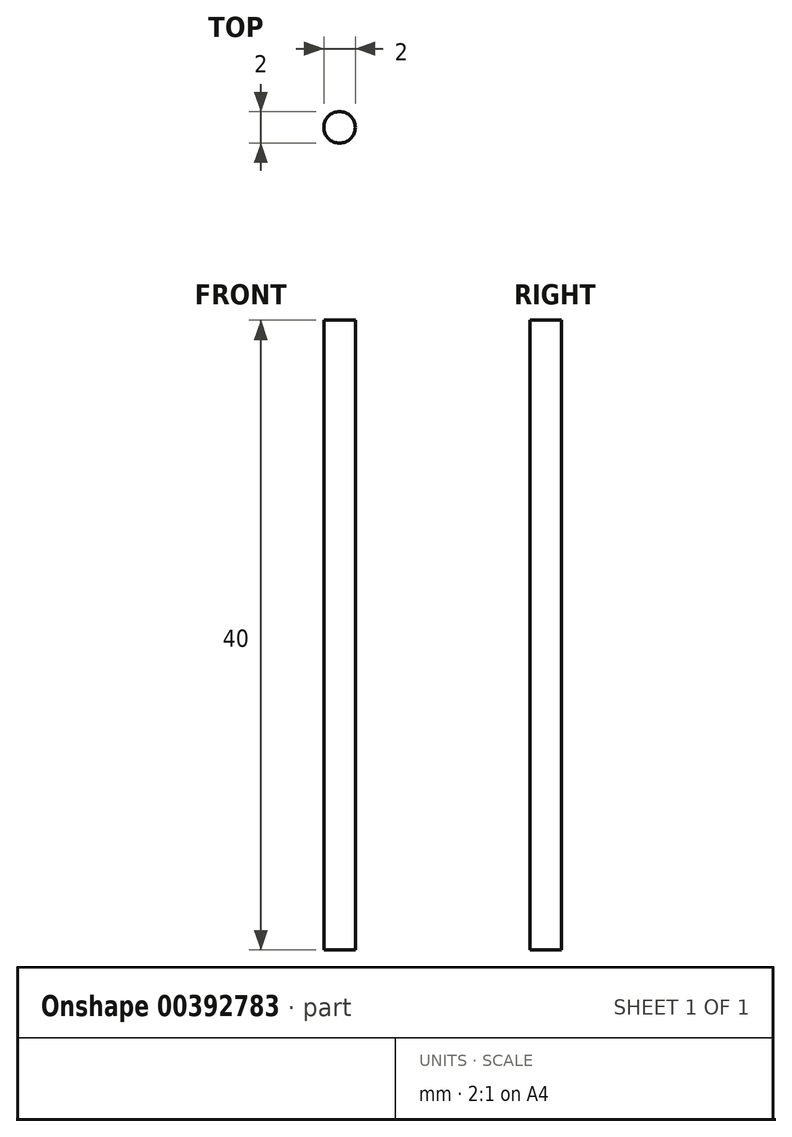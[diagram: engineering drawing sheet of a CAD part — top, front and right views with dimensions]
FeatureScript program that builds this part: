
annotation { "Feature Type Name" : "Feature", "Feature Type Description" : "" }
export const myFeature = defineFeature(function(context is Context, id is Id, definition is map)
    precondition{}
    {
        {
            var Q0;
            Q0=qCreatedBy(makeId("Top.planeOp"),FACE);
            var sketch = newSketch(context, id + "F0", { "sketchPlane" : qUnion([Q0])});
            skCircle(sketch, "E0", {"center": v(0, 0) * mm, "radius": 1 * mm});
            skSolve(sketch);
        }
        {
            var Q0;
            Q0 = qSketchRegion(id + "F0", true);
            extrude(context, id + "F1", {"entities" : qUnion([Q0]), "depth" : 40 * mm});
        }
    });
